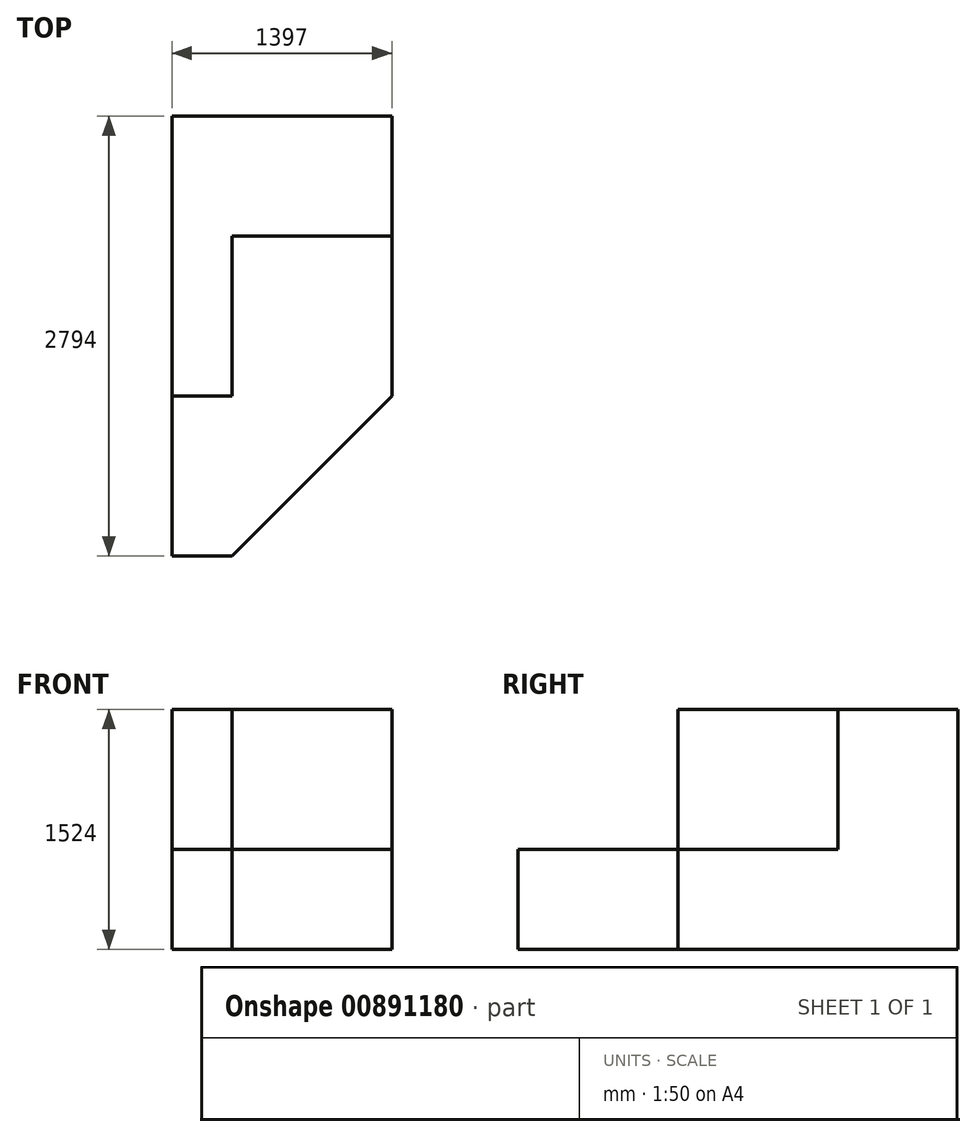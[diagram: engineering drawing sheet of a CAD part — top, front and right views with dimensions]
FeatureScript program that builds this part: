
annotation { "Feature Type Name" : "Feature", "Feature Type Description" : "" }
export const myFeature = defineFeature(function(context is Context, id is Id, definition is map)
    precondition{}
    {
        {
            var Q0;
            Q0=qCreatedBy(makeId("Top.planeOp"),FACE);
            var sketch = newSketch(context, id + "F0", { "sketchPlane" : qUnion([Q0])});
            skLineSegment(sketch, "E0.bottom", {"start": v(0, 0) * mm, "end": v(-1397, 0) * mm});
            skLineSegment(sketch, "E0.top", {"start": v(0, -2794) * mm, "end": v(-1397, -2794) * mm});
            skLineSegment(sketch, "E0.left", {"start": v(0, 0) * mm, "end": v(0, -2794) * mm});
            skLineSegment(sketch, "E0.right", {"start": v(-1397, 0) * mm, "end": v(-1397, -2794) * mm});
            skLineSegment(sketch, "E1", {"start": v(-1397, 0) * mm, "end": v(-1397, -762) * mm});
            skLineSegment(sketch, "E2", {"start": v(-1397, -762) * mm, "end": v(0, -762) * mm});
            skLineSegment(sketch, "E3", {"start": v(-1397, 0) * mm, "end": v(-1016, 0) * mm});
            skLineSegment(sketch, "E4", {"start": v(-1016, 0) * mm, "end": v(-1016, -1778) * mm});
            skLineSegment(sketch, "E5", {"start": v(-1016, -1778) * mm, "end": v(-1397, -1778) * mm});
            skLineSegment(sketch, "E6", {"start": v(0, 0) * mm, "end": v(0, -2149.35) * mm});
            skLineSegment(sketch, "E7", {"start": v(-1397, -2794) * mm, "end": v(-1016, -2794) * mm});
            skLineSegment(sketch, "E8", {"start": v(-1016, -2794) * mm, "end": v(0, -2149.35) * mm});
            skLineSegment(sketch, "E9", {"start": v(0, 0) * mm, "end": v(0, -1778) * mm});
            skLineSegment(sketch, "E10", {"start": v(0, -1778) * mm, "end": v(-1016, -2794) * mm});
            skSolve(sketch);
        }
        {
            var Q0;
            {var subQ3=sQuery(id+"F0.wireOp",EDGE,"E5");Q0=makeQuery(id+"F0.imprint","IMPRINT",FACE,{"disambiguationData":[TD([[makeQuery(id+"F0.imprint","IMPRINT",EDGE,{"derivedFrom":subQ3}),-1.0]])]});}
            var Q1;
            {var subQ0=sQuery(id+"F0.wireOp",EDGE,"E1");Q1=makeQuery(id+"F0.imprint","IMPRINT",FACE,{"disambiguationData":[TD([[makeQuery(id+"F0.imprint","IMPRINT",EDGE,{"derivedFrom":subQ0}),1.0]])]});}
            var Q2;
            {var subQ0=sQuery(id+"F0.wireOp",EDGE,"E0.bottom");Q2=makeQuery(id+"F0.imprint","IMPRINT",FACE,{"disambiguationData":[TD([[makeQuery(id+"F0.imprint","IMPRINT",EDGE,{"derivedFrom":subQ0}),1.0]])]});}
            extrude(context, id + "F1", {"entities" : qUnion([Q0, Q1, Q2]), "depth" : 1524 * mm, "offsetDistance" : 25.4 * mm});
        }
        {
            var Q0;
            {var subQ0=sQuery(id+"F0.wireOp",EDGE,"E5");Q0=makeQuery(id+"F0.imprint","IMPRINT",FACE,{"disambiguationData":[TD([[makeQuery(id+"F0.imprint","IMPRINT",EDGE,{"derivedFrom":subQ0}),1.0]])]});}
            extrude(context, id + "F2", {"entities" : qUnion([Q0]), "operationType" : NewBodyOperationType.ADD, "depth" : 635 * mm, "offsetDistance" : 25.4 * mm});
        }
    });
